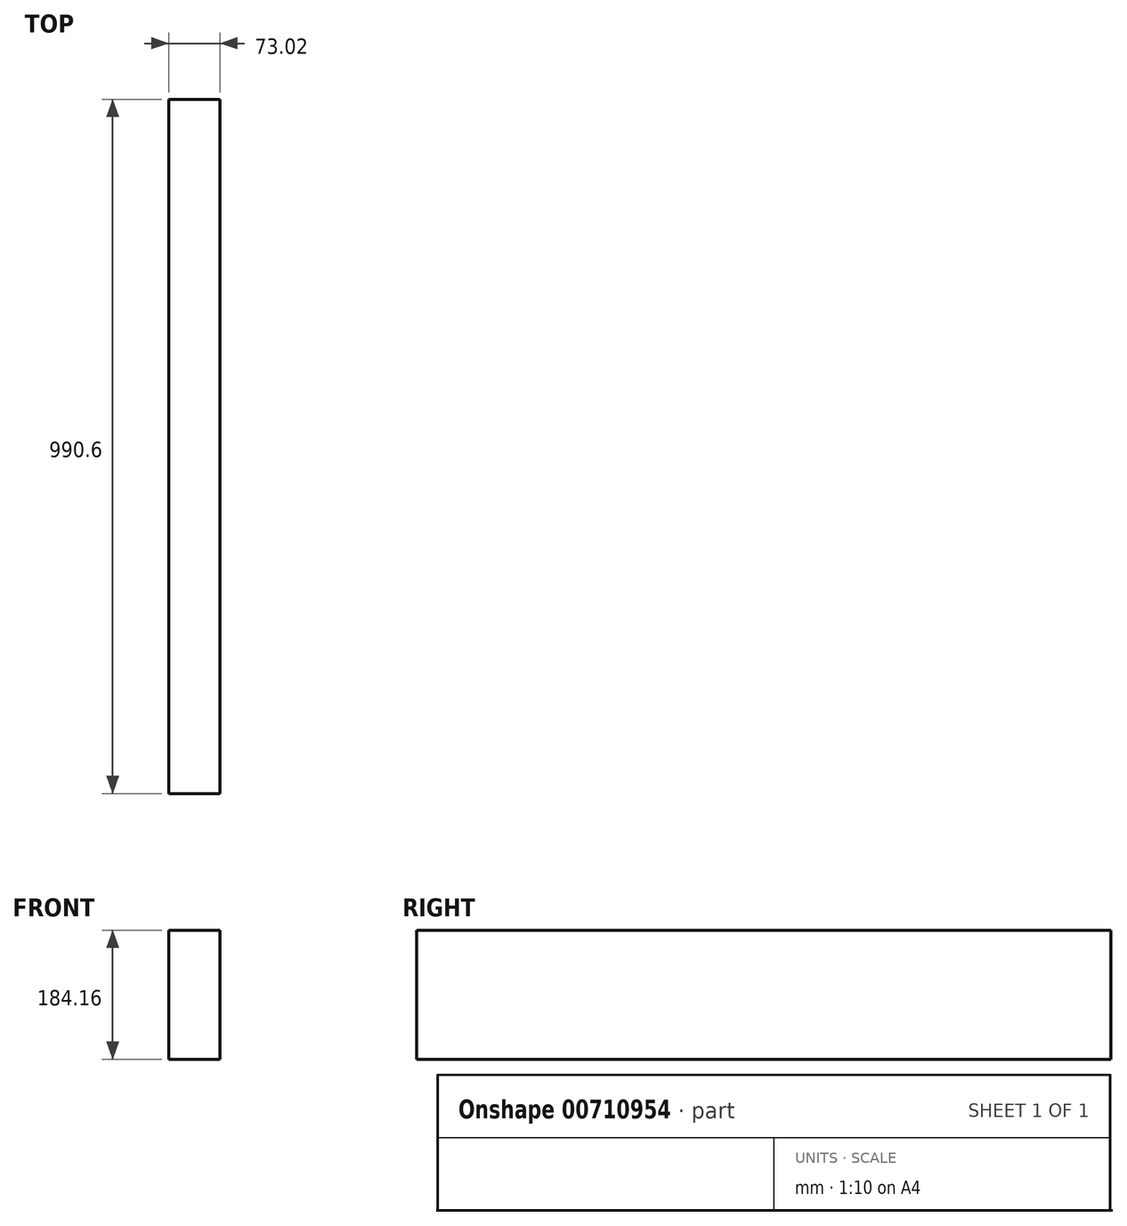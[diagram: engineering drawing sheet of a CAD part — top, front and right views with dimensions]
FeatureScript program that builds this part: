
annotation { "Feature Type Name" : "Feature", "Feature Type Description" : "" }
export const myFeature = defineFeature(function(context is Context, id is Id, definition is map)
    precondition{}
    {
        {
            var Q0;
            Q0=qCreatedBy(makeId("Front.planeOp"),FACE);
            var sketch = newSketch(context, id + "F0", { "sketchPlane" : qUnion([Q0])});
            skLineSegment(sketch, "E0.bottom", {"start": v(-36.51, 92.08) * mm, "end": v(36.51, 92.08) * mm});
            skLineSegment(sketch, "E0.top", {"start": v(-36.51, -92.08) * mm, "end": v(36.51, -92.08) * mm});
            skLineSegment(sketch, "E0.left", {"start": v(-36.51, 92.08) * mm, "end": v(-36.51, -92.08) * mm});
            skLineSegment(sketch, "E0.right", {"start": v(36.51, 92.08) * mm, "end": v(36.51, -92.08) * mm});
            skPoint(sketch, "E0.middle", {"position": v(0, 0) * mm});
            skSolve(sketch);
        }
        {
            var Q0;
            Q0 = qSketchRegion(id + "F0", true);
            extrude(context, id + "F1", {"entities" : qUnion([Q0]), "depth" : 990.6 * mm, "offsetDistance" : 25.4 * mm});
        }
    });
